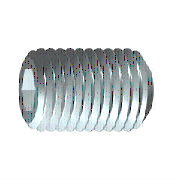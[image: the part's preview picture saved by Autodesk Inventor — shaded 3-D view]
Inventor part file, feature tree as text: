
AUTODESK INVENTOR PART (.ipt)
format: ipt  version: 2020 (Build 240168000, 168)  size: 178,176 bytes
history: native  units: mm (DEFAULTED — no unit token found)
features: sketch x2, extrude x1, other x1, plane x1
ambient origin geometry x8: Origin, YZ Plane, XZ Plane, XY Plane, X Axis, Y Axis, Z Axis, Center Point
bodies: Solid1 (feature_tree), Body (feature_tree)
feature tree (5):
  extrude  "Slot"  TaperAngle=60.0deg  [1 undecoded]
  other  "Work Axis1"
  plane  "Work Plane1"
  sketch  "Sketch1"  dims[d0=1.5mm d1=60.0deg]
  sketch  "Sketch2"  dims[d2=4.0mm d3=2.309401mm d6=90.0deg d4=5.0mm d5=60.0deg d7=2.0mm d8=1.5mm d9=0.0mm d10=1.0mm d11=60.0deg d12=0.429415mm d13=60.0deg d14=5.0mm d15=0.0mm d16=0.0mm d33=1.0mm d34=0.429415mm d35=0.0mm d37=0.0mm]
note: 1 required parameter value undecoded (feature->parameter linkage not recoverable at this tier; creation-order binding heuristic only, values carry confidence <= 0.55)
